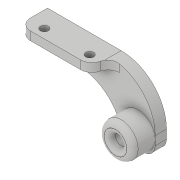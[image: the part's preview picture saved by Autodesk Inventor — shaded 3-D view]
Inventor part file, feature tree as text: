
AUTODESK INVENTOR PART (.ipt)
format: ipt  version: 2018 (Build 220112000, 112)  size: 185,856 bytes
history: native  units: in
note: dims shown in document units (in); Inventor stores cm internally (conversion verified against a paired STEP export)
features: fillet x7, sketch x5, extrude x3, hole x2, plane x1
ambient origin geometry x8: Origin, YZ Plane, XZ Plane, XY Plane, X Axis, Y Axis, Z Axis, Center Point
bodies: Solid1 (feature_tree)
feature tree (18):
  extrude  "Extrusion1"  Depth=1.0in
  hole  "Hole1"  [1 undecoded]
  extrude  "Extrusion2"  Depth=0.25in
  fillet  "Fillet1"  Radius=0.5in
  fillet  "Fillet2"  Radius=0.25in
  extrude  "Extrusion3"  Depth=0.125in
  fillet  "Fillet3"  Radius=0.1875in
  fillet  "Fillet4"  Radius=0.375in
  hole  "Hole2"  [1 undecoded]
  fillet  "Fillet5"  Radius=0.25in
  fillet  "Fillet6"  Radius=1.0in
  fillet  "Fillet7"  Radius=0.894in
  plane  "Work Plane1"
  sketch  "Sketch1"  dims[d0=2.625in d3=1.0in]
  sketch  "Sketch2"  dims[d4=1.069in d5=0.0in]
  sketch  "Sketch3"  dims[d8=0.25in d9=0.0in d12=1.069in]
  sketch  "Sketch4"  dims[d13=0.2461in d14=0.75in d15=0.375in d16=0.25in d17=0.5635in d18=1.0in d19=0.8108in d20=0.5in d21=0.0in d22=0.25in]
  sketch  "Sketch5"  dims[d23=1.0in d24=0.644in d25=0.1875in d26=0.375in d27=0.0in d28=0.25in d29=0.25in d30=1.0in d31=0.894in d32=0.177in d33=0.75in d34=0.332in d35=0.25in d36=0.5635in d37=1.0in d38=0.8108in d39=0.25in d41=1.894in d42=0.75in d43=0.375in d44=0.375in d45=0.375in d46=0.375in d47=0.125in d48=0.125in d49=0.01in]
note: 2 required parameter values undecoded (feature->parameter linkage not recoverable at this tier; creation-order binding heuristic only, values carry confidence <= 0.55)
